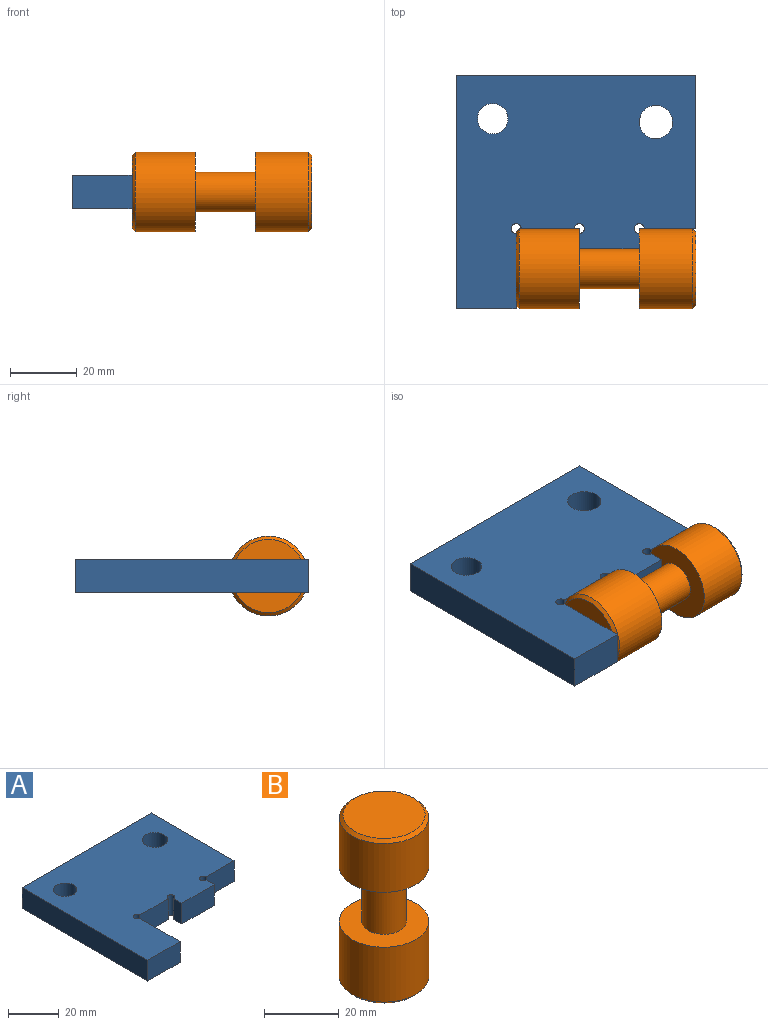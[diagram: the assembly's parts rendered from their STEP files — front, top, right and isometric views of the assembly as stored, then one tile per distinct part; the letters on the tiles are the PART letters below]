
ASSEMBLY  parts=2 mates=1
PART A: 17 faces, bbox 72x70x10 mm
  f0: cylinder r=1.5mm len=10mm, axis (0,0,-1), area 70.7mm2, adj f1,f13,f15,f16
  f1: plane 16x10mm, normal (0,-1,0), area 160mm2, adj f0,f2,f15,f16
  f2: cylinder r=1.5mm len=10mm, axis (0,0,-1), area 70.7mm2, adj f1,f3,f15,f16
  f3: plane 10x4.5mm, normal (-1,0,0), area 45mm2, adj f2,f4,f15,f16
  f4: plane 18x10mm, normal (0,-1,0), area 180mm2, adj f3,f5,f15,f16
  f5: plane 10x4.5mm, normal (1,0,0), area 45mm2, adj f4,f6,f15,f16
  f6: cylinder r=1.5mm len=10mm, axis (0,0,-1), area 70.7mm2, adj f5,f7,f15,f16
  f7: plane 15.5x10mm, normal (0,-1,0), area 155mm2, adj f6,f8,f15,f16
  f8: plane 46x10mm, normal (1,0,0), area 460mm2, adj f7,f9,f15,f16
  f9: plane 72x10mm, normal (0,1,0), area 720mm2, adj f8,f10,f15,f16
  f10: plane 70x10mm, normal (-1,0,0), area 700mm2, adj f9,f11,f15,f16
  f11: plane 18x10mm, normal (0,-1,0), area 180mm2, adj f10,f13,f15,f16
  f12: cylinder r=5mm len=10mm, axis (0,0,-1), area 314.2mm2, adj f15,f16
  f13: plane 22.5x10mm, normal (1,0,0), area 225mm2, adj f0,f11,f15,f16
  f14: cylinder r=4.58mm len=10mm, axis (0,0,-1), area 287.5mm2, adj f15,f16
  f15: plane 72x70mm, normal (0,0,1), area 3691.8mm2, adj f0,f1,f2,f3,f4,f5,f6,f7
  f16: plane 72x70mm, normal (0,0,-1), area 3691.8mm2, adj f0,f1,f2,f3,f4,f5,f6,f7
PART B: 9 faces, bbox 24x24x54 mm
  f0: cylinder r=12mm len=24mm, axis (0,0,-1), area 1357.2mm2, adj f1,f8
  f1: plane 24x24mm, normal (0,0,1), area 339.3mm2, adj f0,f3
  f2: plane 22x22mm, normal (0,0,-1), area 380.1mm2, adj f8
  f3: cylinder r=6mm len=18mm, axis (0,0,-1), area 678.6mm2, adj f1,f6
  f4: cylinder r=12mm len=24mm, axis (0,0,-1), area 1206.4mm2, adj f6,f7
  f5: plane 22x22mm, normal (0,0,1), area 380.1mm2, adj f7
  f6: plane 24x24mm, normal (0,0,-1), area 339.3mm2, adj f3,f4
  f7: cone r=11mm half-angle=45deg, axis (0,0,-1), area 102.2mm2, adj f4,f5
  f8: cone r=12mm half-angle=45deg, axis (0,0,1), area 102.2mm2, adj f0,f2
PLACE A t=(58.74,-79.03,44.81)mm
PLACE B rot(axis=(0.71,0,0.71),180deg) t=(-60.07,22.07,105.86)mm
MATE fastened B.f0 <-> A.f13  axis (-1,0,0) through (-60.07,-14.09,49.81)mm
